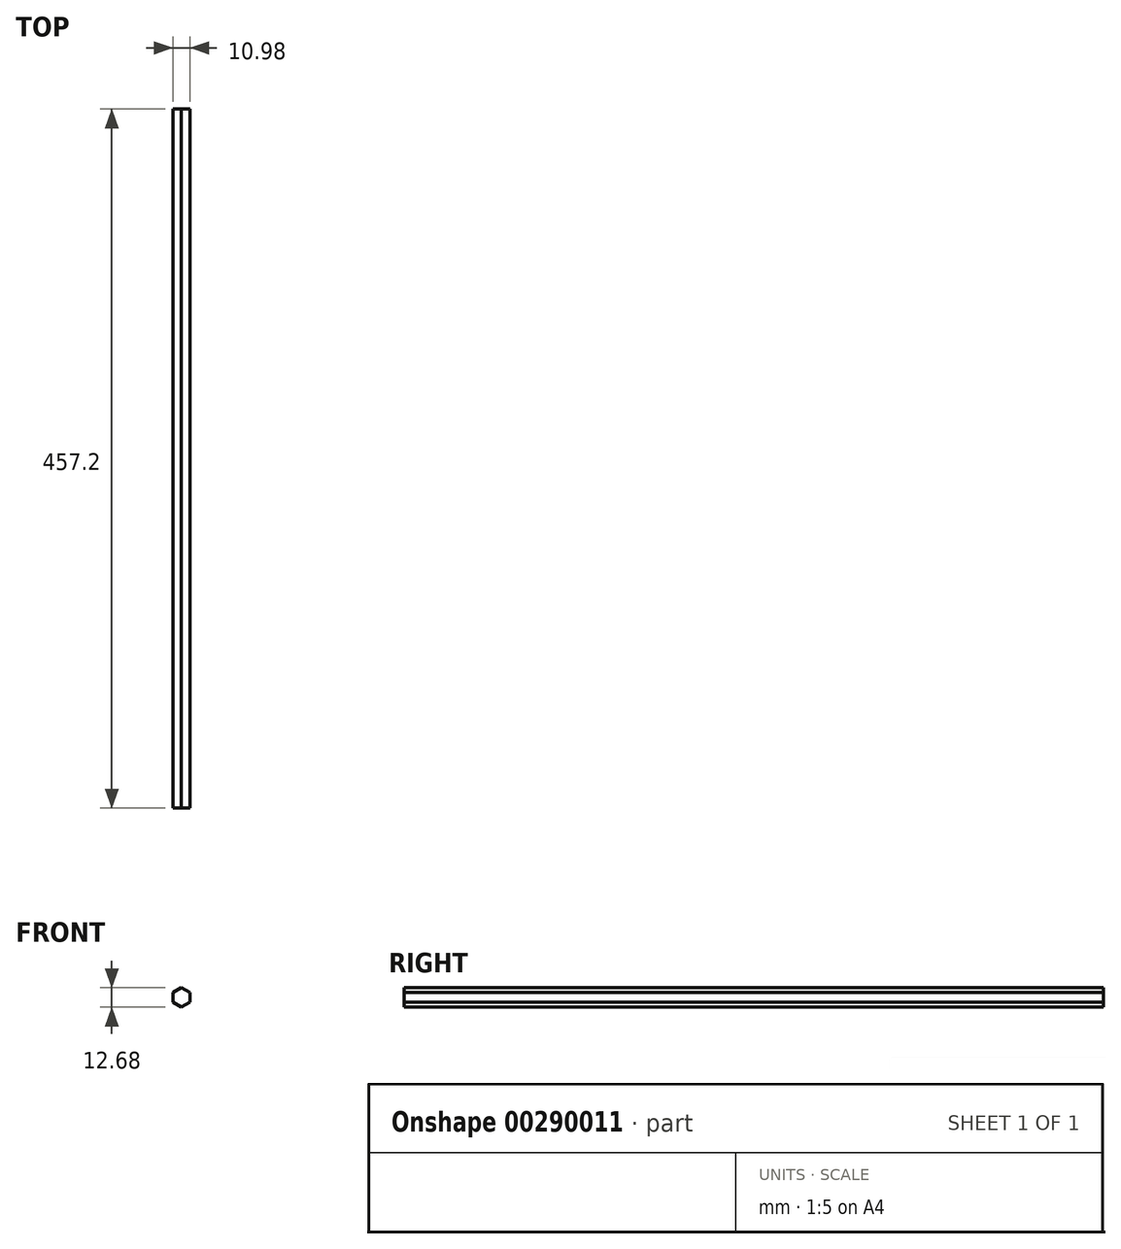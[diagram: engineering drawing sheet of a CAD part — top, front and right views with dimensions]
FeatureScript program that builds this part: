
annotation { "Feature Type Name" : "Feature", "Feature Type Description" : "" }
export const myFeature = defineFeature(function(context is Context, id is Id, definition is map)
    precondition{}
    {
        {
            var Q0;
            Q0=qCreatedBy(makeId("Front.planeOp"),FACE);
            var sketch = newSketch(context, id + "F0", { "sketchPlane" : qUnion([Q0])});
            skCircle(sketch, "E0.cCircle", {"center": v(0, 0) * mm, "radius": 5.5 * mm, "construction": true});
            skLineSegment(sketch, "E0.0", {"start": v(5.5, 3.17) * mm, "end": v(5.5, -3.17) * mm});
            skLineSegment(sketch, "E0.1", {"start": v(5.5, -3.17) * mm, "end": v(0, -6.34) * mm});
            skLineSegment(sketch, "E0.2", {"start": v(0, -6.34) * mm, "end": v(-5.5, -3.17) * mm});
            skLineSegment(sketch, "E0.3", {"start": v(-5.5, -3.17) * mm, "end": v(-5.5, 3.17) * mm});
            skLineSegment(sketch, "E0.4", {"start": v(-5.5, 3.17) * mm, "end": v(0, 6.34) * mm});
            skLineSegment(sketch, "E0.5", {"start": v(0, 6.34) * mm, "end": v(5.5, 3.17) * mm});
            skPoint(sketch, "E0.0.midPoint", {"position": v(5.5, 0) * mm});
            skSolve(sketch);
        }
        {
            var Q0;
            Q0 = qSketchRegion(id + "F0", true);
            extrude(context, id + "F1", {"entities" : qUnion([Q0]), "depth" : 457.2 * mm});
        }
    });
